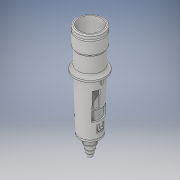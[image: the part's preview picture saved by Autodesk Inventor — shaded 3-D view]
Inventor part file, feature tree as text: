
AUTODESK INVENTOR PART (.ipt)
format: ipt  version: 2019.1 (Build 231200000, 200)  size: 798,720 bytes
history: native  units: mm
features: sketch x18, extrude x16, fillet x6, plane x3, revolve x2
ambient origin geometry x8: Origin, YZ Plane, XZ Plane, XY Plane, X Axis, Y Axis, Z Axis, Center Point
bodies: Solid1 (feature_tree)
feature tree (45):
  extrude  "Extrusion1"  Depth=18.6mm
  extrude  "Extrusion2"  Depth=22.5mm
  fillet  "Fillet1"  Radius=15.5mm
  plane  "Work Plane1"
  extrude  "Extrusion3"  [1 undecoded]
  fillet  "Fillet2"  Radius=0.3mm
  fillet  "Fillet3"  Radius=1.0mm
  extrude  "Extrusion4"  Depth=1.5mm
  fillet  "Fillet4"  Radius=1.5mm
  revolve  "Revolution1"  Angle=90.0deg
  extrude  "Extrusion5"  Depth=1.5mm
  revolve  "Revolution2"  [1 undecoded]
  sketch  "Sketch8"  dims[d24=90.0deg d25=3.1mm d26=5.0mm]
  extrude  "Extrusion6"  Depth=3.1mm
  fillet  "Fillet5"  Radius=5.0mm
  extrude  "Extrusion7"  Depth=1.5mm
  plane  "Work Plane2"
  extrude  "Extrusion8"  Depth=10.0mm
  extrude  "Extrusion9"  Depth=5.7mm
  plane  "Work Plane3"
  extrude  "Extrusion10"  Depth=5.0mm TaperAngle=0.0deg
  extrude  "Extrusion11"  [1 undecoded]
  extrude  "Extrusion12"  Depth=5.8mm
  extrude  "Extrusion13"  Depth=2.9mm
  extrude  "Extrusion15"  Depth=2.5mm TaperAngle=0.0deg
  extrude  "Extrusion16"  Depth=11.8mm
  fillet  "Fillet6"  Radius=5.9mm
  extrude  "Extrusion17"  Depth=13.8mm
  sketch  "Sketch1"  dims[d0=20.5mm d1=18.6mm]
  sketch  "Sketch2"  dims[d2=32.0mm d3=0.0mm d4=22.5mm d5=15.5mm d6=0.0mm]
  sketch  "Sketch3"  dims[d7=1.0mm d8=-3.3mm d9=0.3mm d10=0.0mm d11=1.0mm]
  sketch  "Sketch4"  dims[d12=1.0mm d13=25.5mm d14=1.5mm d15=0.0mm]
  sketch  "Sketch5"  dims[d16=3.0mm d18=90.0deg]
  sketch  "Sketch6"  dims[d19=1.5mm d20=0.0mm d21=16.0mm]
  sketch  "Sketch7"  dims[d22=4.0mm d23=2.0mm]
  sketch  "Sketch9"  dims[d27=32.0mm d28=0.0mm d29=1.5mm]
  sketch  "Sketch10"  dims[d30=70.0mm d31=0.0mm d32=10.0mm]
  sketch  "Sketch11"  dims[d34=5.6mm d35=5.7mm]
  sketch  "Sketch12"  dims[d36=2.8mm d40=5.0mm d41=0.0mm]
  sketch  "Sketch13"  dims[d42=2.5mm d43=0.0mm d44=-20.0mm]
  sketch  "Sketch14"  dims[d45=6.8mm d46=5.8mm]
  sketch  "Sketch15"  dims[d47=5.8mm d48=2.9mm]
  sketch  "Sketch16"  dims[d49=3.0mm d50=0.0mm d51=2.5mm d52=0.0mm]
  sketch  "Sketch17"  dims[d53=8.6mm d54=11.8mm d55=5.9mm]
  sketch  "Sketch18"  dims[d56=2.5mm d57=13.8mm d58=4.6mm d59=0.85mm d60=5.0mm d61=0.0mm d62=13.8mm d63=4.8mm d64=7.4mm d65=1.0mm d69=5.0mm d70=0.0mm d73=2.0mm d74=0.0mm d75=5.5mm d76=1.8mm d77=0.5mm d78=0.5mm d79=0.0mm d80=3.0mm d81=50.0mm d82=0.0mm d83=3.1mm]
note: 3 required parameter values undecoded (feature->parameter linkage not recoverable at this tier; creation-order binding heuristic only, values carry confidence <= 0.55)